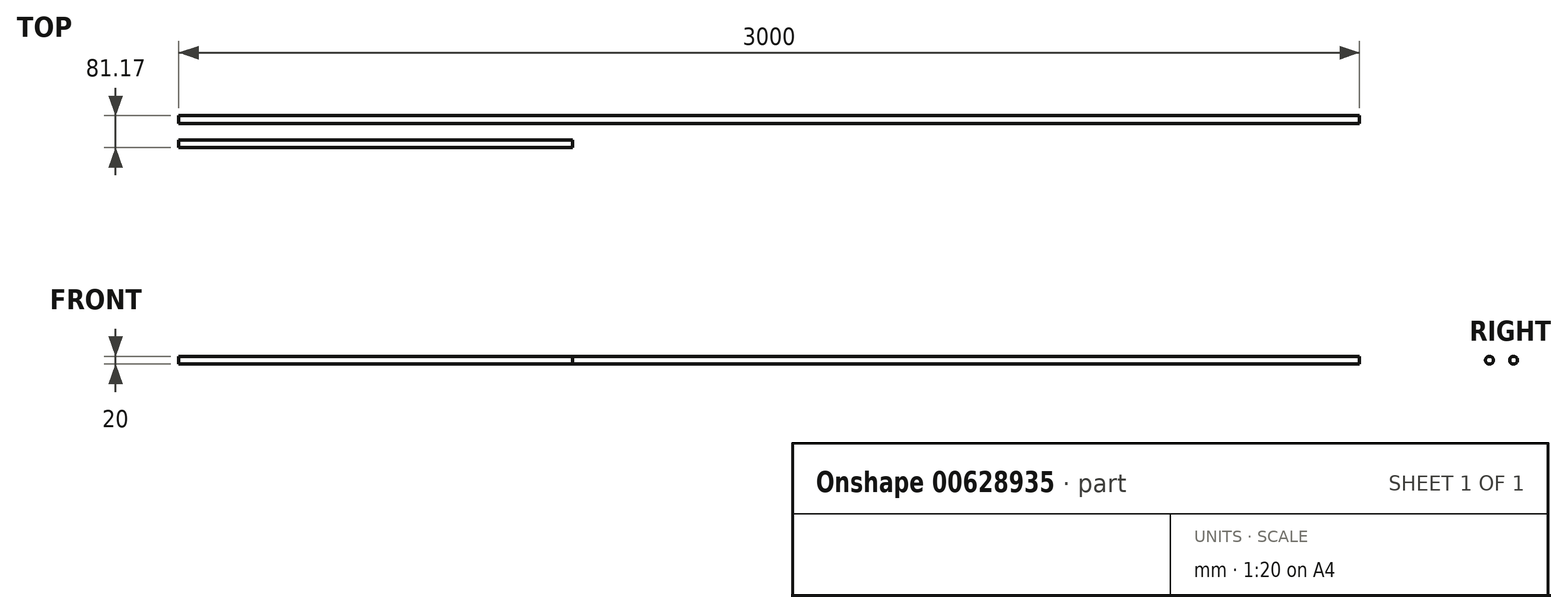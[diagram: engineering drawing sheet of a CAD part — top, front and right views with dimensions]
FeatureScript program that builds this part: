
annotation { "Feature Type Name" : "Feature", "Feature Type Description" : "" }
export const myFeature = defineFeature(function(context is Context, id is Id, definition is map)
    precondition{}
    {
        {
            var Q0;
            Q0=qCreatedBy(makeId("Right.planeOp"),FACE);
            var sketch = newSketch(context, id + "F0", { "sketchPlane" : qUnion([Q0])});
            skCircle(sketch, "E0", {"center": v(0, 0) * mm, "radius": 10 * mm});
            skSolve(sketch);
        }
        {
            var Q0;
            Q0=makeQuery(id+"F0.imprint","IMPRINT",FACE,{"disambiguationData":[TD([[makeQuery(id+"F0.imprint","IMPRINT",EDGE,{"derivedFrom":sQuery(id+"F0.wireOp",EDGE,"E0")}),1.0]])]});
            extrude(context, id + "F1", {"entities" : qUnion([Q0]), "depth" : 3000 * mm, "offsetDistance" : 25 * mm});
        }
        {
            var Q0;
            Q0=qCreatedBy(makeId("Right.planeOp"),FACE);
            var sketch = newSketch(context, id + "F2", { "sketchPlane" : qUnion([Q0])});
            skCircle(sketch, "E1", {"center": v(-61.17, 0) * mm, "radius": 10 * mm});
            skSolve(sketch);
        }
        {
            var Q0;
            Q0=makeQuery(id+"F2.imprint","IMPRINT",FACE,{"disambiguationData":[TD([[makeQuery(id+"F2.imprint","IMPRINT",EDGE,{"derivedFrom":sQuery(id+"F2.wireOp",EDGE,"E1")}),1.0]])]});
            extrude(context, id + "F3", {"entities" : qUnion([Q0]), "depth" : 1000 * mm, "offsetDistance" : 25 * mm});
        }
    });
